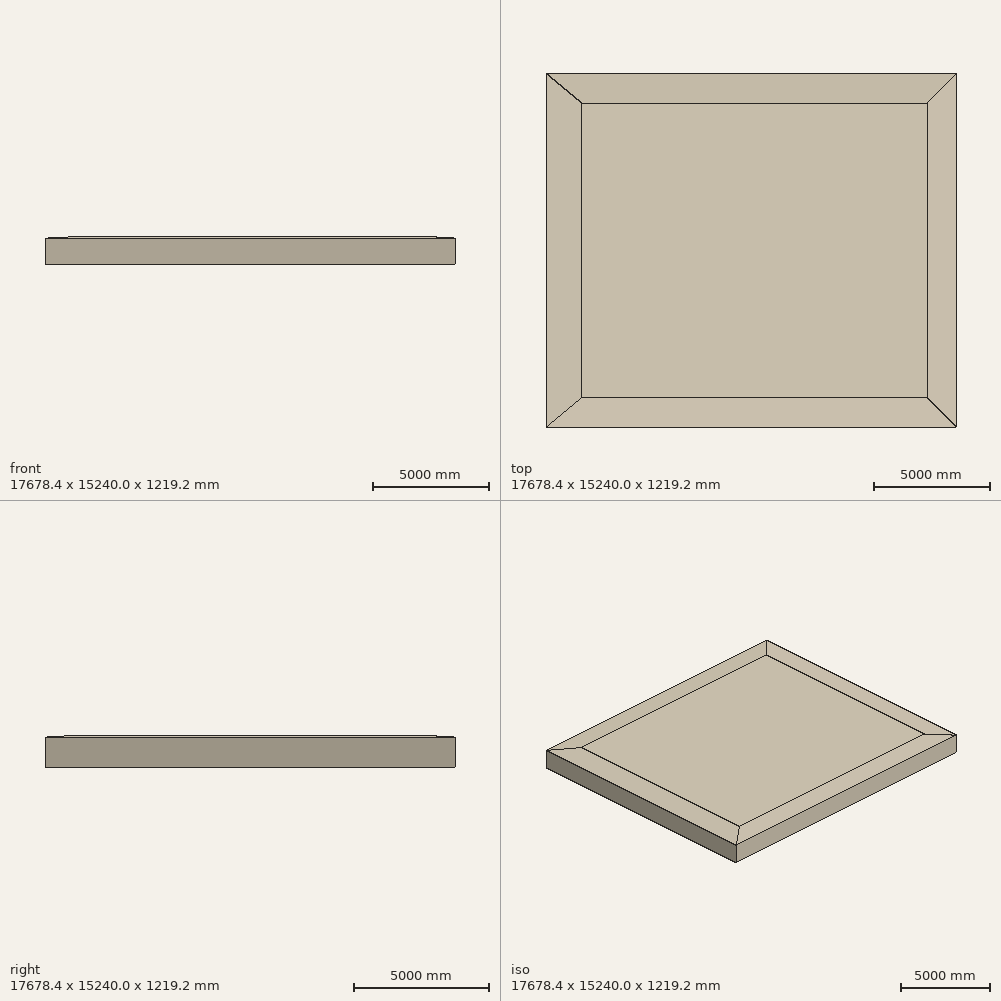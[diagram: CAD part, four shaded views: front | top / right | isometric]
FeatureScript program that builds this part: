
annotation { "Feature Type Name" : "Feature", "Feature Type Description" : "" }
export const myFeature = defineFeature(function(context is Context, id is Id, definition is map)
    precondition{}
    {
        {
            var Q0;
            Q0=qCreatedBy(makeId("Top.planeOp"),FACE);
            var sketch = newSketch(context, id + "F0", { "sketchPlane" : qUnion([Q0])});
            skLineSegment(sketch, "E0.bottom", {"start": v(0, 15240) * mm, "end": v(17678.4, 15240) * mm});
            skLineSegment(sketch, "E0.top", {"start": v(0, 0) * mm, "end": v(17678.4, 0) * mm});
            skLineSegment(sketch, "E0.left", {"start": v(0, 15240) * mm, "end": v(0, 0) * mm});
            skLineSegment(sketch, "E0.right", {"start": v(17678.4, 15240) * mm, "end": v(17678.4, 0) * mm});
            skSolve(sketch);
        }
        {
            var Q0;
            Q0=makeQuery(id+"F0.imprint","IMPRINT",FACE,{"disambiguationData":[TD([[makeQuery(id+"F0.imprint","IMPRINT",EDGE,{"derivedFrom":sQuery(id+"F0.wireOp",EDGE,"E0.bottom")}),-1.0]])]});
            extrude(context, id + "F1", {"entities" : qUnion([Q0]), "depth" : 1219.2 * mm});
        }
        {
            var Q0;
            Q0=makeQuery(id+"F1.opExtrude","SWEPT_FACE",FACE,{"disambiguationData":[OSD([sQuery(id+"F0.wireOp",EDGE,"E0.top")])]});
            var sketch = newSketch(context, id + "F2", { "sketchPlane" : qUnion([Q0])});
            skLineSegment(sketch, "E1", {"start": v(0, 1143) * mm, "end": v(1524, 1219.2) * mm});
            skSolve(sketch);
        }
        {
            var Q0;
            {var subQ0=sQuery(id+"F2.wireOp",EDGE,"E1");Q0=makeQuery(id+"F2.imprint","IMPRINT",FACE,{"disambiguationData":[TD([[makeQuery(id+"F2.imprint","IMPRINT",EDGE,{"derivedFrom":subQ0}),1.0]])]});}
            extrude(context, id + "F3", {"entities" : qUnion([Q0]), "operationType" : NewBodyOperationType.REMOVE, "endBound" : BoundingType.THROUGH_ALL, "oppositeDirection" : true, "depth" : 25.4 * mm});
        }
        {
            var Q0;
            Q0=makeQuery(id+"F1.opExtrude","CAP_EDGE",EDGE,{"disambiguationData":[OSD([sQuery(id+"F0.wireOp",EDGE,"E0.top")])],"isStart":false});
            var Q1;
            Q1=makeQuery(id+"F1.opExtrude","CAP_EDGE",EDGE,{"disambiguationData":[OSD([sQuery(id+"F0.wireOp",EDGE,"E0.right")])],"isStart":false});
            var Q2;
            Q2=makeQuery(id+"F1.opExtrude","CAP_EDGE",EDGE,{"disambiguationData":[OSD([sQuery(id+"F0.wireOp",EDGE,"E0.bottom")])],"isStart":false});
            chamfer(context, id + "F4", {"entities" : qUnion([Q0, Q1, Q2]), "chamferType" : ChamferType.TWO_OFFSETS, "width1" : 1270 * mm, "oppositeDirection" : false, "width2" : 76.2 * mm, "tangentPropagation" : true});
        }
    });
